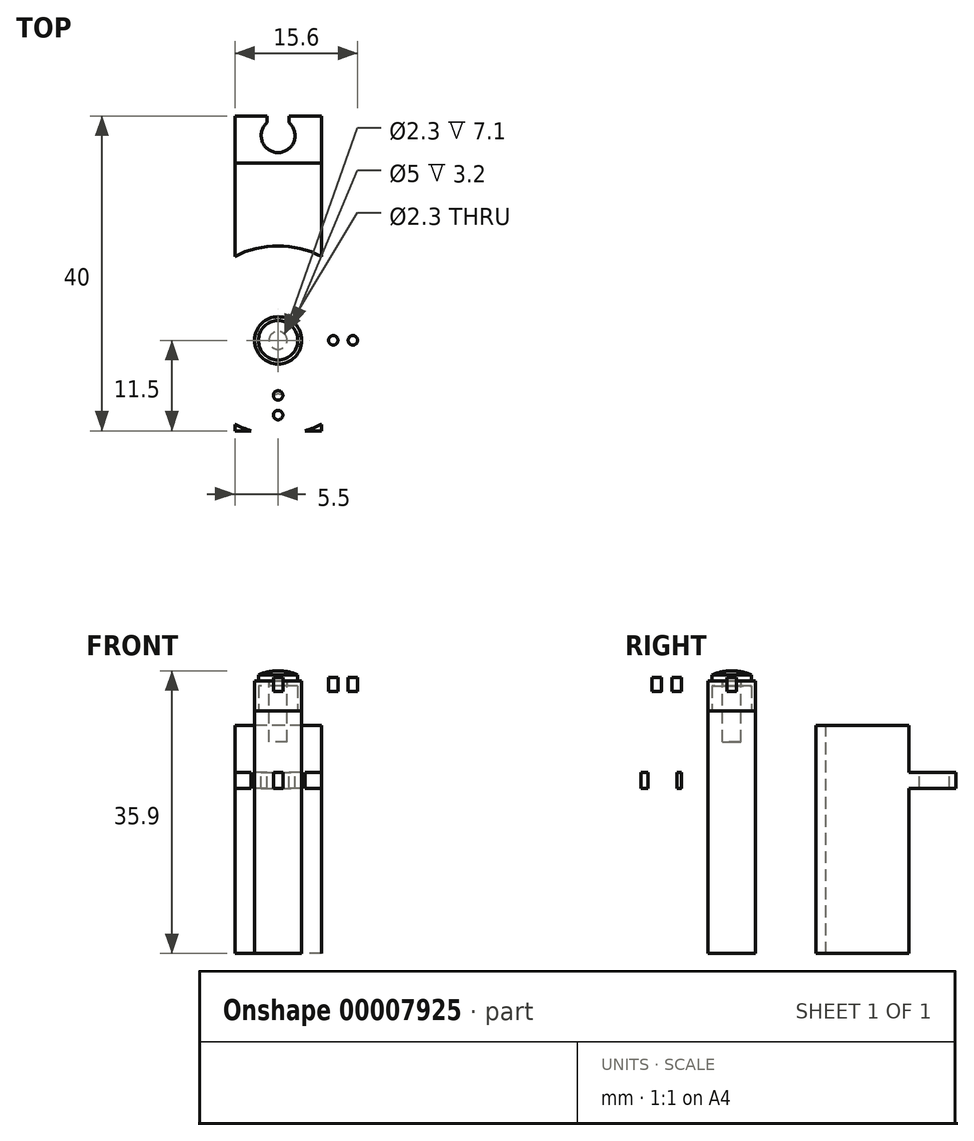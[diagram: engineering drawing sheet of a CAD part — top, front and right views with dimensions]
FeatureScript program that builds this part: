
annotation { "Feature Type Name" : "Feature", "Feature Type Description" : "" }
export const myFeature = defineFeature(function(context is Context, id is Id, definition is map)
    precondition{}
    {
        {
            var Q0;
            Q0=qCreatedBy(makeId("Right.planeOp"),FACE);
            var sketch = newSketch(context, id + "F0", { "sketchPlane" : qUnion([Q0])});
            skLineSegment(sketch, "E0.bottom", {"start": v(-5.5, 8) * mm, "end": v(22.5, 8) * mm});
            skLineSegment(sketch, "E0.top", {"start": v(-5.5, -21) * mm, "end": v(22.5, -21) * mm});
            skLineSegment(sketch, "E0.left", {"start": v(-5.5, 8) * mm, "end": v(-5.5, 2) * mm});
            skLineSegment(sketch, "E0.right", {"start": v(22.5, 8) * mm, "end": v(22.5, 2) * mm});
            skLineSegment(sketch, "E1.bottom", {"start": v(-11.5, 2) * mm, "end": v(-5.5, 2) * mm});
            skLineSegment(sketch, "E1.top", {"start": v(-11.5, 0) * mm, "end": v(-5.5, 0) * mm});
            skLineSegment(sketch, "E1.left", {"start": v(-11.5, 2) * mm, "end": v(-11.5, 0) * mm});
            skLineSegment(sketch, "E1.right", {"start": v(28.5, 2) * mm, "end": v(28.5, 0) * mm});
            skLineSegment(sketch, "E2.trimOffspring", {"start": v(22.5, 2) * mm, "end": v(28.5, 2) * mm});
            skLineSegment(sketch, "E3.trimOffspring", {"start": v(22.5, 0) * mm, "end": v(28.5, 0) * mm});
            skLineSegment(sketch, "E4.trimOffspring", {"start": v(-5.5, 0) * mm, "end": v(-5.5, -21) * mm});
            skLineSegment(sketch, "E5.trimOffspring", {"start": v(22.5, 0) * mm, "end": v(22.5, -21) * mm});
            skSolve(sketch);
        }
        {
            var Q0;
            Q0=qSketchRegion(id+"F0",true);
            extrude(context, id + "F1", {"entities" : qUnion([Q0]), "endBound" : BoundingType.SYMMETRIC, "depth" : 11 * mm});
        }
        {
            var Q0;
            Q0=makeQuery(id+"F1.opExtrude","SWEPT_FACE",FACE,{"disambiguationData":[OSD([sQuery(id+"F0.wireOp",EDGE,"E1.bottom")])]});
            var sketch = newSketch(context, id + "F2", { "sketchPlane" : qUnion([Q0])});
            skArc(sketch, "E6", {"start": v(1.4, -10.63) * mm, "mid": v(0, -6.85) * mm, "end": v(-1.4, -10.63) * mm});
            skArc(sketch, "E7", {"start": v(-1.4, 27.63) * mm, "mid": v(0, 23.85) * mm, "end": v(1.4, 27.63) * mm});
            skLineSegment(sketch, "E8", {"start": v(0, 26) * mm, "end": v(0, -9) * mm, "construction": true});
            skLineSegment(sketch, "E9", {"start": v(1.4, -10.63) * mm, "end": v(1.4, -11.5) * mm});
            skLineSegment(sketch, "E10", {"start": v(1.4, -11.5) * mm, "end": v(-1.4, -11.5) * mm});
            skLineSegment(sketch, "E11", {"start": v(-1.4, -11.5) * mm, "end": v(-1.4, -10.63) * mm});
            skLineSegment(sketch, "E12", {"start": v(-1.4, 27.63) * mm, "end": v(-1.4, 28.5) * mm});
            skLineSegment(sketch, "E13", {"start": v(-1.4, 28.5) * mm, "end": v(1.4, 28.5) * mm});
            skLineSegment(sketch, "E14", {"start": v(1.4, 28.5) * mm, "end": v(1.4, 27.63) * mm});
            skLineSegment(sketch, "E15", {"start": v(0, -9) * mm, "end": v(0, -11.5) * mm, "construction": true});
            skLineSegment(sketch, "E16", {"start": v(0, 26) * mm, "end": v(0, 28.5) * mm, "construction": true});
            skSolve(sketch);
        }
        {
            var Q0;
            Q0=qSketchRegion(id+"F2",true);
            extrude(context, id + "F3", {"entities" : qUnion([Q0]), "operationType" : NewBodyOperationType.REMOVE, "endBound" : BoundingType.THROUGH_ALL, "oppositeDirection" : true, "depth" : 25 * mm});
        }
        {
            var Q0;
            Q0=makeQuery(id+"F1.opExtrude","SWEPT_FACE",FACE,{"disambiguationData":[OSD([sQuery(id+"F0.wireOp",EDGE,"E0.bottom")])]});
            var sketch = newSketch(context, id + "F4", { "sketchPlane" : qUnion([Q0])});
            skArc(sketch, "E17", {"start": v(-2, 4.58) * mm, "mid": v(0, -5) * mm, "end": v(2, 4.58) * mm});
            skArc(sketch, "E18", {"start": v(2, 5.5) * mm, "mid": v(0, 7.5) * mm, "end": v(-2, 5.5) * mm});
            skLineSegment(sketch, "E19", {"start": v(0, 0) * mm, "end": v(0, 5.5) * mm, "construction": true});
            skLineSegment(sketch, "E20", {"start": v(-2, 5.5) * mm, "end": v(-2, 4.58) * mm});
            skLineSegment(sketch, "E21.0.MirrorCS", {"start": v(2, 5.5) * mm, "end": v(2, 4.58) * mm});
            skSolve(sketch);
        }
        {
            var Q0;
            Q0=qSketchRegion(id+"F4",true);
            extrude(context, id + "F5", {"entities" : qUnion([Q0]), "operationType" : NewBodyOperationType.ADD, "depth" : 1.8 * mm});
        }
        {
            var Q0;
            Q0=makeQuery(id+"F5.opExtrude","CAP_FACE",FACE,{"disambiguationData":[OSD([sQuery(id+"F4.wireOp",EDGE,"E17"),sQuery(id+"F4.wireOp",EDGE,"E18"),sQuery(id+"F4.wireOp",EDGE,"E20"),sQuery(id+"F4.wireOp",EDGE,"E21.0.MirrorCS")])],"isStart":false});
            var sketch = newSketch(context, id + "F6", { "sketchPlane" : qUnion([Q0])});
            skCircle(sketch, "E22", {"center": v(0, 0) * mm, "radius": 2.5 * mm});
            skSolve(sketch);
        }
        {
            var Q0;
            Q0=qSketchRegion(id+"F6",true);
            extrude(context, id + "F7", {"entities" : qUnion([Q0]), "operationType" : NewBodyOperationType.ADD, "depth" : 3.2 * mm});
        }
        {
            var Q0;
            Q0=makeQuery(id+"F1.opExtrude","SWEPT_FACE",FACE,{"disambiguationData":[OSD([sQuery(id+"F0.wireOp",EDGE,"E4.trimOffspring")])]});
            var sketch = newSketch(context, id + "F8", { "sketchPlane" : qUnion([Q0])});
            skLineSegment(sketch, "E23.bottom", {"start": v(-1.5, -21) * mm, "end": v(1.5, -21) * mm});
            skLineSegment(sketch, "E23.top", {"start": v(-1.5, -19.2) * mm, "end": v(1.5, -19.2) * mm});
            skLineSegment(sketch, "E23.left", {"start": v(-1.5, -21) * mm, "end": v(-1.5, -19.2) * mm});
            skLineSegment(sketch, "E23.right", {"start": v(1.5, -21) * mm, "end": v(1.5, -19.2) * mm});
            skLineSegment(sketch, "E24", {"start": v(0, 0) * mm, "end": v(0, -21) * mm, "construction": true});
            skSolve(sketch);
        }
        {
            var Q0;
            Q0=qSketchRegion(id+"F8",true);
            extrude(context, id + "F9", {"entities" : qUnion([Q0]), "operationType" : NewBodyOperationType.REMOVE, "oppositeDirection" : true, "depth" : 1.8 * mm});
        }
        {
            var Q0;
            Q0=makeQuery(id+"F7.opExtrude","CAP_FACE",FACE,{"disambiguationData":[OSD([sQuery(id+"F6.wireOp",EDGE,"E22")])],"isStart":false});
            var sketch = newSketch(context, id + "F10", { "sketchPlane" : qUnion([Q0])});
            skCircle(sketch, "E25", {"center": v(0, 0) * mm, "radius": 1.15 * mm});
            skSolve(sketch);
        }
        {
            var Q0;
            Q0=qSketchRegion(id+"F10",true);
            extrude(context, id + "F11", {"entities" : qUnion([Q0]), "operationType" : NewBodyOperationType.REMOVE, "oppositeDirection" : true, "depth" : 7.1 * mm});
        }
        {
            var Q0;
            Q0=qCreatedBy(makeId("Right.planeOp"),FACE);
            var sketch = newSketch(context, id + "F12", { "sketchPlane" : qUnion([Q0])});
            skLineSegment(sketch, "E26", {"start": v(-4, 12.3) * mm, "end": v(-4, 9.8) * mm});
            skLineSegment(sketch, "E27", {"start": v(-4, 9.8) * mm, "end": v(-2.5, 9.8) * mm});
            skLineSegment(sketch, "E28", {"start": v(-2.5, 9.8) * mm, "end": v(-2.5, 13) * mm});
            skLineSegment(sketch, "E29", {"start": v(-2.5, 13) * mm, "end": v(-1.15, 13) * mm});
            skLineSegment(sketch, "E30", {"start": v(-1.15, 13) * mm, "end": v(-1.15, 13.6) * mm});
            skLineSegment(sketch, "E31", {"start": v(-1.15, 13.6) * mm, "end": v(-3, 13.6) * mm});
            skLineSegment(sketch, "E32", {"start": v(-3, 13.6) * mm, "end": v(-3, 14.1) * mm});
            skLineSegment(sketch, "E33", {"start": v(-3, 14.1) * mm, "end": v(-12, 14.1) * mm});
            skLineSegment(sketch, "E34", {"start": v(-12, 14.1) * mm, "end": v(-12, 12.3) * mm});
            skLineSegment(sketch, "E35", {"start": v(-12, 12.3) * mm, "end": v(-4, 12.3) * mm});
            skLineSegment(sketch, "E36", {"start": v(0, 0) * mm, "end": v(0, 17.16) * mm, "construction": true});
            skSolve(sketch);
        }
        {
            var Q0;
            Q0=qSketchRegion(id+"F12",true);
            var Q1;
            Q1=sQuery(id+"F12.wireOp",EDGE,"E36");
            revolve(context, id + "F13", {"entities" : qUnion([Q0]), "axis" : qUnion([Q1]), "revolveType" : RevolveType.FULL});
        }
        {
            var Q0;
            Q0=makeQuery(id+"F13.opRevolve","SWEPT_FACE",FACE,{"disambiguationData":[OSD([sQuery(id+"F12.wireOp",EDGE,"E33")])]});
            var sketch = newSketch(context, id + "F14", { "sketchPlane" : qUnion([Q0])});
            skLineSegment(sketch, "E37", {"start": v(0, 0) * mm, "end": v(-9.5, 0) * mm, "construction": true});
            skCircle(sketch, "E38", {"center": v(-9.5, 0) * mm, "radius": 0.6 * mm});
            skCircle(sketch, "E39", {"center": v(-7, 0) * mm, "radius": 0.6 * mm});
            skArc(sketch, "E40", {"start": v(-3.12, -2.5) * mm, "mid": v(-2.83, -2.83) * mm, "end": v(-2.5, -3.12) * mm});
            skLineSegment(sketch, "E41", {"start": v(-9.5, -2.5) * mm, "end": v(-3.12, -2.5) * mm});
            skLineSegment(sketch, "E42", {"start": v(-9.5, 2.5) * mm, "end": v(-3.12, 2.5) * mm});
            skArc(sketch, "E43.trimOffspring", {"start": v(-9.5, 2.5) * mm, "mid": v(-12, 0) * mm, "end": v(-9.5, -2.5) * mm});
            skLineSegment(sketch, "E44", {"start": v(0, 0) * mm, "end": v(0, 9.5) * mm, "construction": true});
            skCircle(sketch, "E45", {"center": v(0, 9.5) * mm, "radius": 0.6 * mm});
            skCircle(sketch, "E46", {"center": v(0, 7) * mm, "radius": 0.6 * mm});
            skLineSegment(sketch, "E47", {"start": v(-2.5, 9.5) * mm, "end": v(-2.5, 3.12) * mm});
            skLineSegment(sketch, "E48", {"start": v(2.5, 9.5) * mm, "end": v(2.5, 3.12) * mm});
            skArc(sketch, "E49.trimOffspring", {"start": v(2.5, 9.5) * mm, "mid": v(0, 12) * mm, "end": v(-2.5, 9.5) * mm});
            skLineSegment(sketch, "E50.0.MirrorCS", {"start": v(9.5, -2.5) * mm, "end": v(3.12, -2.5) * mm});
            skCircle(sketch, "E50.1.MirrorC", {"center": v(7, 0) * mm, "radius": 0.6 * mm});
            skCircle(sketch, "E50.2.MirrorC", {"center": v(9.5, 0) * mm, "radius": 0.6 * mm});
            skLineSegment(sketch, "E50.3.MirrorCS", {"start": v(9.5, 2.5) * mm, "end": v(3.12, 2.5) * mm});
            skArc(sketch, "E50.4.MirrorCS", {"start": v(9.5, 2.5) * mm, "mid": v(12, 0) * mm, "end": v(9.5, -2.5) * mm});
            skCircle(sketch, "E51.0.MirrorC", {"center": v(0, -9.5) * mm, "radius": 0.6 * mm});
            skCircle(sketch, "E51.1.MirrorC", {"center": v(0, -7) * mm, "radius": 0.6 * mm});
            skLineSegment(sketch, "E51.2.MirrorCS", {"start": v(2.5, -9.5) * mm, "end": v(2.5, -3.12) * mm});
            skLineSegment(sketch, "E51.3.MirrorCS", {"start": v(-2.5, -9.5) * mm, "end": v(-2.5, -3.12) * mm});
            skArc(sketch, "E51.4.MirrorCS", {"start": v(2.5, -9.5) * mm, "mid": v(0, -12) * mm, "end": v(-2.5, -9.5) * mm});
            skArc(sketch, "E52.trimOffspring", {"start": v(2.5, -3.12) * mm, "mid": v(2.83, -2.83) * mm, "end": v(3.12, -2.5) * mm});
            skArc(sketch, "E53.trimOffspring", {"start": v(3.12, 2.5) * mm, "mid": v(2.83, 2.83) * mm, "end": v(2.5, 3.12) * mm});
            skArc(sketch, "E54.trimOffspring", {"start": v(-2.5, 3.12) * mm, "mid": v(-2.83, 2.83) * mm, "end": v(-3.12, 2.5) * mm});
            skSolve(sketch);
        }
        {
            var Q0;
            Q0=makeQuery(id+"F14.imprint","IMPRINT",FACE,{"disambiguationData":[TD([[makeQuery(id+"F14.imprint","IMPRINT",EDGE,{"derivedFrom":sQuery(id+"F14.wireOp",EDGE,"E40")}),-1.0]])]});
            var Q1;
            {var subQ6=sQuery(id+"F14.wireOp",EDGE,"E42");Q1=makeQuery(id+"F14.imprint","IMPRINT",FACE,{"disambiguationData":[TD([[makeQuery(id+"F14.imprint","IMPRINT",EDGE,{"derivedFrom":subQ6}),1.0]])]});}
            var Q2;
            {var subQ6=sQuery(id+"F14.wireOp",EDGE,"E50.0.MirrorCS");Q2=makeQuery(id+"F14.imprint","IMPRINT",FACE,{"disambiguationData":[TD([[makeQuery(id+"F14.imprint","IMPRINT",EDGE,{"derivedFrom":subQ6}),1.0]])]});}
            var Q3;
            {var subQ6=sQuery(id+"F14.wireOp",EDGE,"E48");Q3=makeQuery(id+"F14.imprint","IMPRINT",FACE,{"disambiguationData":[TD([[makeQuery(id+"F14.imprint","IMPRINT",EDGE,{"derivedFrom":subQ6}),1.0]])]});}
            var Q4;
            Q4=makeQuery(id+"F14.imprint","IMPRINT",FACE,{"disambiguationData":[TD([[makeQuery(id+"F14.imprint","IMPRINT",EDGE,{"derivedFrom":sQuery(id+"F14.wireOp",EDGE,"E38")}),1.0]])]});
            var Q5;
            Q5=makeQuery(id+"F14.imprint","IMPRINT",FACE,{"disambiguationData":[TD([[makeQuery(id+"F14.imprint","IMPRINT",EDGE,{"derivedFrom":sQuery(id+"F14.wireOp",EDGE,"E39")}),1.0]])]});
            var Q6;
            Q6=makeQuery(id+"F14.imprint","IMPRINT",FACE,{"disambiguationData":[TD([[makeQuery(id+"F14.imprint","IMPRINT",EDGE,{"derivedFrom":sQuery(id+"F14.wireOp",EDGE,"E46")}),1.0]])]});
            var Q7;
            Q7=makeQuery(id+"F14.imprint","IMPRINT",FACE,{"disambiguationData":[TD([[makeQuery(id+"F14.imprint","IMPRINT",EDGE,{"derivedFrom":sQuery(id+"F14.wireOp",EDGE,"E45")}),1.0]])]});
            var Q8;
            Q8=makeQuery(id+"F14.imprint","IMPRINT",FACE,{"disambiguationData":[TD([[makeQuery(id+"F14.imprint","IMPRINT",EDGE,{"derivedFrom":sQuery(id+"F14.wireOp",EDGE,"E50.2.MirrorC")}),-1.0]])]});
            var Q9;
            Q9=makeQuery(id+"F14.imprint","IMPRINT",FACE,{"disambiguationData":[TD([[makeQuery(id+"F14.imprint","IMPRINT",EDGE,{"derivedFrom":sQuery(id+"F14.wireOp",EDGE,"E50.1.MirrorC")}),-1.0]])]});
            var Q10;
            Q10=makeQuery(id+"F14.imprint","IMPRINT",FACE,{"disambiguationData":[TD([[makeQuery(id+"F14.imprint","IMPRINT",EDGE,{"derivedFrom":sQuery(id+"F14.wireOp",EDGE,"E51.1.MirrorC")}),-1.0]])]});
            var Q11;
            Q11=makeQuery(id+"F14.imprint","IMPRINT",FACE,{"disambiguationData":[TD([[makeQuery(id+"F14.imprint","IMPRINT",EDGE,{"derivedFrom":sQuery(id+"F14.wireOp",EDGE,"E51.0.MirrorC")}),-1.0]])]});
            var Q12;
            Q12=qSketchRegion(id+"F16",true);
            extrude(context, id + "F15", {"entities" : qUnion([Q0, Q1, Q2, Q3, Q4, Q5, Q6, Q7, Q8, Q9, Q10, Q11, Q12]), "operationType" : NewBodyOperationType.REMOVE, "endBound" : BoundingType.THROUGH_ALL, "oppositeDirection" : true, "depth" : 25 * mm});
        }
        {
            var Q0;
            Q0=qCreatedBy(makeId("Right.planeOp"),FACE);
            var sketch = newSketch(context, id + "F16", { "sketchPlane" : qUnion([Q0])});
            skLineSegment(sketch, "E55", {"start": v(0, 14.9) * mm, "end": v(0, 0) * mm, "construction": true});
            skLineSegment(sketch, "E56", {"start": v(-2.5, 13.6) * mm, "end": v(-2.5, 14.4) * mm});
            skLineSegment(sketch, "E57", {"start": v(-2.5, 13.6) * mm, "end": v(-1.15, 13.6) * mm});
            skLineSegment(sketch, "E58", {"start": v(-1.15, 13.6) * mm, "end": v(-1.15, 5.9) * mm});
            skLineSegment(sketch, "E59", {"start": v(-1.15, 5.9) * mm, "end": v(0, 5.9) * mm});
            skArc(sketch, "E60", {"start": v(0, 14.9) * mm, "mid": v(-1.27, 14.77) * mm, "end": v(-2.5, 14.4) * mm});
            skLineSegment(sketch, "E61", {"start": v(0, 14.9) * mm, "end": v(0, 5.9) * mm});
            skSolve(sketch);
        }
        {
            var Q0;
            Q0=qSketchRegion(id+"F16",true);
            var Q1;
            Q1=sQuery(id+"F16.wireOp",EDGE,"E55");
            revolve(context, id + "F17", {"entities" : qUnion([Q0]), "axis" : qUnion([Q1]), "revolveType" : RevolveType.FULL});
        }
    });
